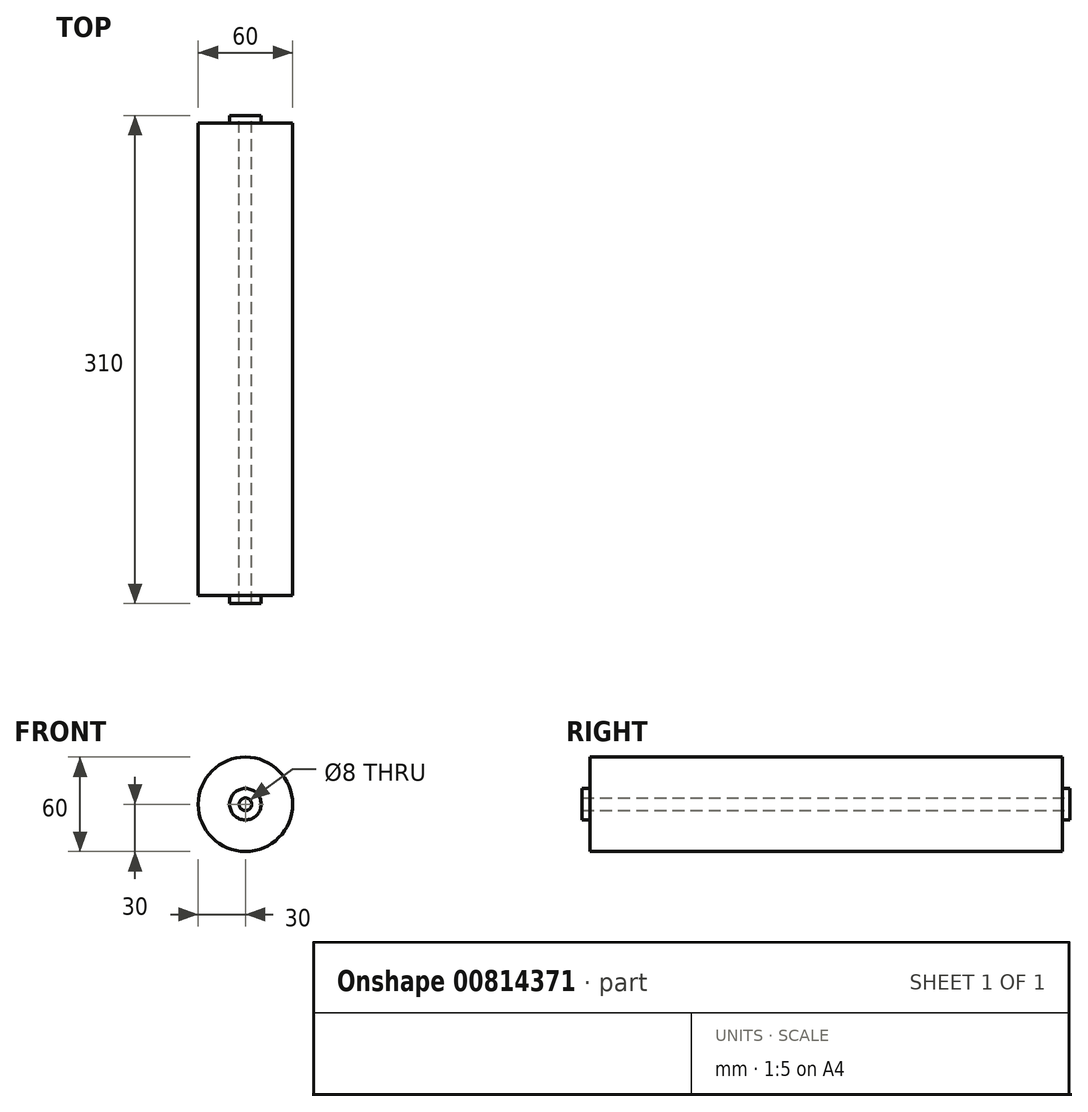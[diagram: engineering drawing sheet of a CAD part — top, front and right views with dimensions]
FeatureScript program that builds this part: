
annotation { "Feature Type Name" : "Feature", "Feature Type Description" : "" }
export const myFeature = defineFeature(function(context is Context, id is Id, definition is map)
    precondition{}
    {
        {
            var Q0;
            Q0=qCreatedBy(makeId("Front.planeOp"),FACE);
            var sketch = newSketch(context, id + "F0", { "sketchPlane" : qUnion([Q0])});
            skCircle(sketch, "E0", {"center": v(0, 0) * mm, "radius": 30 * mm});
            skCircle(sketch, "E1", {"center": v(0, 0) * mm, "radius": 4 * mm});
            skSolve(sketch);
        }
        {
            var Q0;
            Q0=makeQuery(id+"F0.imprint","IMPRINT",FACE,{"disambiguationData":[TD([[makeQuery(id+"F0.imprint","IMPRINT",EDGE,{"derivedFrom":sQuery(id+"F0.wireOp",EDGE,"E0")}),1.0]])]});
            extrude(context, id + "F1", {"entities" : qUnion([Q0]), "depth" : 300 * mm, "offsetDistance" : 25 * mm});
        }
        {
            var Q0;
            Q0=makeQuery(id+"F1.opExtrude","CAP_FACE",FACE,{"disambiguationData":[OSD([sQuery(id+"F0.wireOp",EDGE,"E0"),sQuery(id+"F0.wireOp",EDGE,"E1")])],"isStart":false});
            var sketch = newSketch(context, id + "F2", { "sketchPlane" : qUnion([Q0])});
            skCircle(sketch, "E2", {"center": v(0, 0) * mm, "radius": 10 * mm});
            skSolve(sketch);
        }
        {
            var Q0;
            Q0=makeQuery(id+"F2.imprint","IMPRINT",FACE,{"disambiguationData":[TD([[makeQuery(id+"F2.imprint","IMPRINT",EDGE,{"derivedFrom":sQuery(id+"F2.wireOp",EDGE,"E2")}),1.0]])]});
            extrude(context, id + "F3", {"entities" : qUnion([Q0]), "operationType" : NewBodyOperationType.ADD, "depth" : 5 * mm, "offsetDistance" : 25 * mm});
        }
        {
            var Q0;
            Q0=makeQuery(id+"F1.opExtrude","CAP_FACE",FACE,{"disambiguationData":[OSD([sQuery(id+"F0.wireOp",EDGE,"E0"),sQuery(id+"F0.wireOp",EDGE,"E1")])],"isStart":true});
            var sketch = newSketch(context, id + "F4", { "sketchPlane" : qUnion([Q0])});
            skCircle(sketch, "E3", {"center": v(0, 0) * mm, "radius": 10 * mm});
            skSolve(sketch);
        }
        {
            var Q0;
            Q0=makeQuery(id+"F4.imprint","IMPRINT",FACE,{"disambiguationData":[TD([[makeQuery(id+"F4.imprint","IMPRINT",EDGE,{"derivedFrom":sQuery(id+"F4.wireOp",EDGE,"E3")}),1.0]])]});
            extrude(context, id + "F5", {"entities" : qUnion([Q0]), "operationType" : NewBodyOperationType.ADD, "depth" : 5 * mm, "offsetDistance" : 25 * mm});
        }
    });
